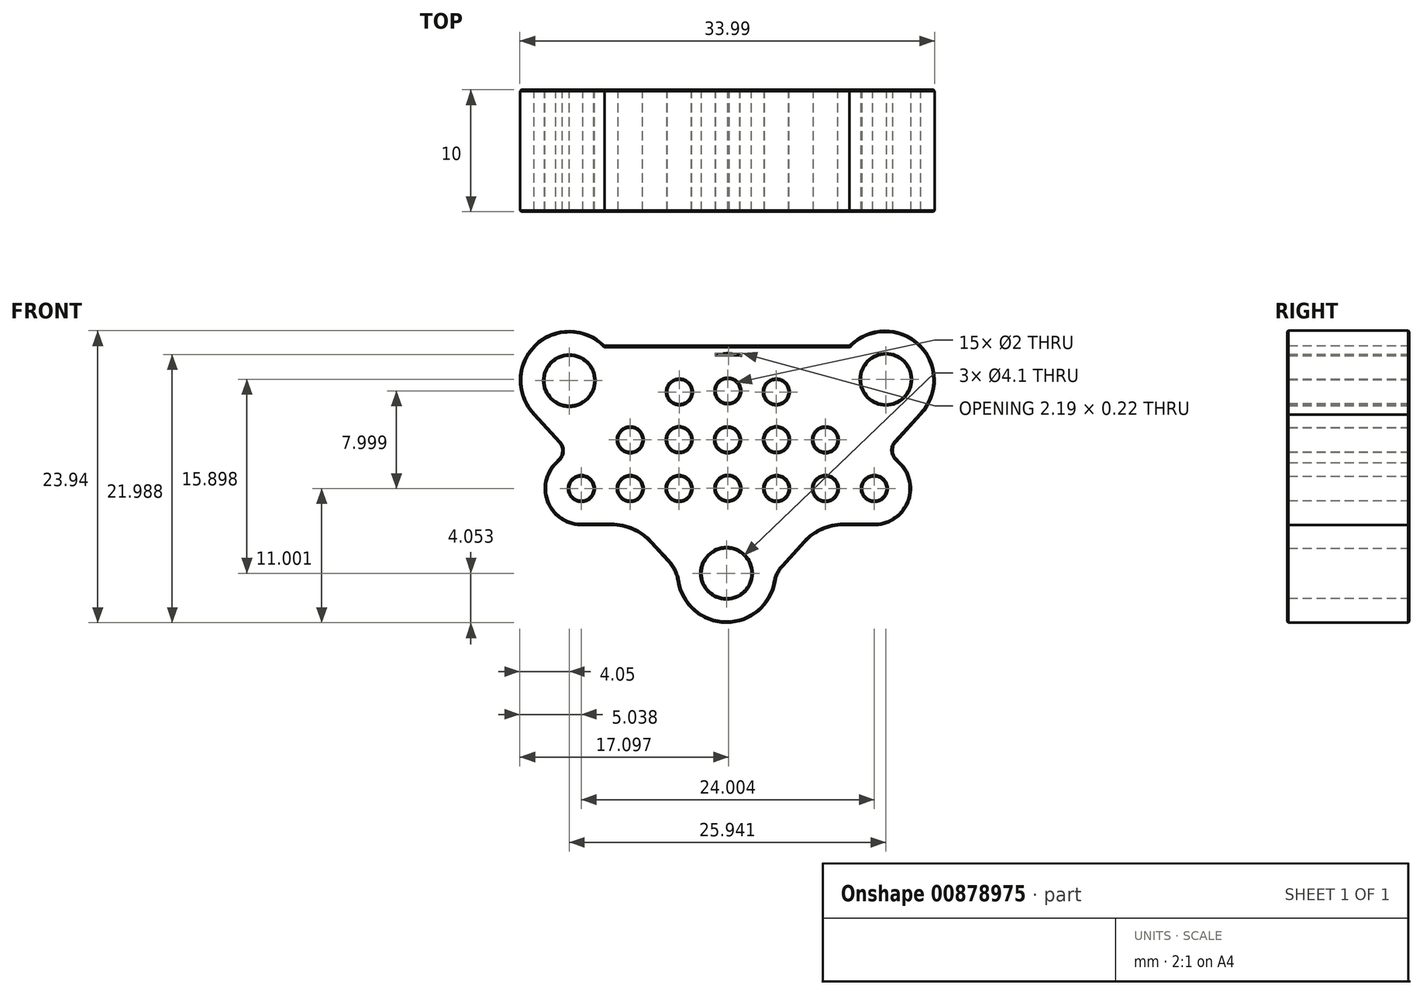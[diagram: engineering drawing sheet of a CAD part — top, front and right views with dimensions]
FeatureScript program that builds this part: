
annotation { "Feature Type Name" : "Feature", "Feature Type Description" : "" }
export const myFeature = defineFeature(function(context is Context, id is Id, definition is map)
    precondition{}
    {
        {
            var Q0;
            Q0=qCreatedBy(makeId("Front.planeOp"),FACE);
            var sketch = newSketch(context, id + "F0", { "sketchPlane" : qUnion([Q0])});
            skLineSegment(sketch, "E0", {"start": v(0, 0) * mm, "end": v(12, 0) * mm, "construction": true});
            skLineSegment(sketch, "E1.0", {"start": v(0, -4) * mm, "end": v(12, -4) * mm, "construction": true});
            skLineSegment(sketch, "E2", {"start": v(0, 4) * mm, "end": v(0, -4) * mm, "construction": true});
            skLineSegment(sketch, "E3.0", {"start": v(4, 4) * mm, "end": v(4, -4) * mm, "construction": true});
            skLineSegment(sketch, "E4.0", {"start": v(8, 4) * mm, "end": v(8, -4) * mm, "construction": true});
            skLineSegment(sketch, "E5.0", {"start": v(12, 0) * mm, "end": v(12, -4) * mm, "construction": true});
            skLineSegment(sketch, "E6.0", {"start": v(0, 4) * mm, "end": v(8, 4) * mm, "construction": true});
            skCircle(sketch, "E7", {"center": v(0, 4) * mm, "radius": 1 * mm});
            skCircle(sketch, "E8", {"center": v(3.97, 3.92) * mm, "radius": 1 * mm});
            skCircle(sketch, "E9", {"center": v(-0.03, 0) * mm, "radius": 1 * mm});
            skCircle(sketch, "E10", {"center": v(4, 0) * mm, "radius": 1 * mm});
            skCircle(sketch, "E11", {"center": v(8, 0) * mm, "radius": 1 * mm});
            skCircle(sketch, "E12", {"center": v(0, -3.98) * mm, "radius": 1 * mm});
            skCircle(sketch, "E13", {"center": v(4, -4) * mm, "radius": 1 * mm});
            skCircle(sketch, "E14", {"center": v(8, -4) * mm, "radius": 1 * mm});
            skCircle(sketch, "E15", {"center": v(12, -4) * mm, "radius": 1 * mm});
            skArc(sketch, "E16.0", {"start": v(11.88, -7) * mm, "mid": v(14.75, -5.2) * mm, "end": v(14.1, -1.86) * mm});
            skLineSegment(sketch, "E17", {"start": v(0, 7) * mm, "end": v(0.12, 7) * mm});
            skLineSegment(sketch, "E18", {"start": v(12.12, -7) * mm, "end": v(9.45, -7) * mm});
            skArc(sketch, "E19.trimOffspring", {"start": v(0.12, 7) * mm, "mid": v(0.06, 7) * mm, "end": v(0, 7) * mm});
            skCircle(sketch, "E20.MirrorC", {"center": v(-4, -4) * mm, "radius": 1 * mm});
            skCircle(sketch, "E21.MirrorC", {"center": v(-8, -4) * mm, "radius": 1 * mm});
            skCircle(sketch, "E22.MirrorC", {"center": v(-12, -4) * mm, "radius": 1 * mm});
            skLineSegment(sketch, "E23.MirrorCS", {"start": v(-4, 4) * mm, "end": v(-4, -4) * mm, "construction": true});
            skCircle(sketch, "E24.MirrorC", {"center": v(-4, 0) * mm, "radius": 1 * mm});
            skLineSegment(sketch, "E25.MirrorCS", {"start": v(-12, 0) * mm, "end": v(-12, -4) * mm, "construction": true});
            skLineSegment(sketch, "E26.MirrorCS", {"start": v(-8, 4) * mm, "end": v(-8, -4) * mm, "construction": true});
            skCircle(sketch, "E27.MirrorC", {"center": v(-3.97, 3.92) * mm, "radius": 1 * mm});
            skCircle(sketch, "E28.MirrorC", {"center": v(-8, 0) * mm, "radius": 1 * mm});
            skArc(sketch, "E29.MirrorCS", {"start": v(-11.88, -7) * mm, "mid": v(-14.75, -5.2) * mm, "end": v(-14.1, -1.86) * mm});
            skLineSegment(sketch, "E30.MirrorCS", {"start": v(-12.12, -7) * mm, "end": v(-9.54, -7) * mm});
            skPoint(sketch, "E31.orphan", {"position": v(3, -4.1) * mm});
            skPoint(sketch, "E32.0.end.orphan", {"position": v(3, -3.88) * mm});
            skPoint(sketch, "E33.MirrorCS.end.orphan", {"position": v(-3, -3.88) * mm});
            skPoint(sketch, "E33.MirrorCS.start.orphan", {"position": v(-3, -4.1) * mm});
            skLineSegment(sketch, "E34.0", {"start": v(12.1, -11) * mm, "end": v(0, -10.98) * mm});
            skCircle(sketch, "E35", {"center": v(-12.99, 4.85) * mm, "radius": 2.05 * mm});
            skCircle(sketch, "E36", {"center": v(12.95, 4.95) * mm, "radius": 2.05 * mm});
            skCircle(sketch, "E37", {"center": v(-0.1, -10.95) * mm, "radius": 2.05 * mm});
            skArc(sketch, "E38.0", {"start": v(-4.1, -11.59) * mm, "mid": v(-0.13, -15) * mm, "end": v(3.88, -11.63) * mm});
            skLineSegment(sketch, "E39", {"start": v(-10.1, 7.7) * mm, "end": v(9.97, 7.7) * mm});
            skLineSegment(sketch, "E40", {"start": v(-15.87, 2.02) * mm, "end": v(-13.82, -0.22) * mm});
            skLineSegment(sketch, "E41", {"start": v(4.5, -10.37) * mm, "end": v(6.32, -8.37) * mm});
            skLineSegment(sketch, "E42.trimOffspring", {"start": v(-13.84, -1.58) * mm, "end": v(-14.1, -1.86) * mm});
            skLineSegment(sketch, "E43.trimOffspring", {"start": v(-6.32, -8.4) * mm, "end": v(-4.88, -9.98) * mm});
            skArc(sketch, "E44.trimOffspring", {"start": v(-10.1, 7.7) * mm, "mid": v(-15.83, 7.75) * mm, "end": v(-15.87, 2.02) * mm});
            skPoint(sketch, "E45.MirrorCS.end.orphan", {"position": v(-4.03, 6.92) * mm});
            skPoint(sketch, "E45.MirrorCS.start.orphan", {"position": v(-6.26, 5.86) * mm});
            skPoint(sketch, "E46.MirrorCS.start.orphan", {"position": v(0, 7) * mm});
            skPoint(sketch, "E47.trimOffspring.end.orphan", {"position": v(4.03, 6.92) * mm});
            skPoint(sketch, "E48.orphan", {"position": v(6.26, 5.86) * mm});
            skArc(sketch, "E49.trimOffspring", {"start": v(15.81, 2.07) * mm, "mid": v(15.7, 7.8) * mm, "end": v(9.97, 7.7) * mm});
            skLineSegment(sketch, "E50.trimOffspring", {"start": v(13.8, -1.57) * mm, "end": v(14.1, -1.86) * mm});
            skLineSegment(sketch, "E51.trimOffspring", {"start": v(13.77, -0.18) * mm, "end": v(15.81, 2.07) * mm});
            skPoint(sketch, "E52.trimOffspring.end.orphan", {"position": v(0, -6.98) * mm});
            skPoint(sketch, "E53.0.start.orphan", {"position": v(-9.07, 8.7) * mm});
            skPoint(sketch, "E54.trimOffspring.end.orphan", {"position": v(-16.91, 1) * mm});
            skPoint(sketch, "E55.visualSharp", {"position": v(-13.2, -0.9) * mm});
            skArc(sketch, "E55.filletArc", {"start": v(-13.84, -1.58) * mm, "mid": v(-13.56, -0.9) * mm, "end": v(-13.82, -0.22) * mm});
            skPoint(sketch, "E56.visualSharp", {"position": v(-7.62, -6.99) * mm});
            skArc(sketch, "E56.filletArc", {"start": v(-6.32, -8.4) * mm, "mid": v(-7.78, -7.36) * mm, "end": v(-9.54, -7) * mm});
            skPoint(sketch, "E57.visualSharp", {"position": v(-4.15, -10.78) * mm});
            skArc(sketch, "E57.filletArc", {"start": v(-4.1, -11.59) * mm, "mid": v(-4.38, -10.73) * mm, "end": v(-4.88, -9.98) * mm});
            skPoint(sketch, "E58.visualSharp", {"position": v(13.12, -0.9) * mm});
            skArc(sketch, "E58.filletArc", {"start": v(13.77, -0.18) * mm, "mid": v(13.5, -0.88) * mm, "end": v(13.8, -1.57) * mm});
            skPoint(sketch, "E59.visualSharp", {"position": v(7.57, -6.99) * mm});
            skArc(sketch, "E59.filletArc", {"start": v(9.45, -7) * mm, "mid": v(7.73, -7.35) * mm, "end": v(6.32, -8.37) * mm});
            skPoint(sketch, "E60.visualSharp", {"position": v(3.94, -10.98) * mm});
            skArc(sketch, "E60.filletArc", {"start": v(4.5, -10.37) * mm, "mid": v(4.1, -10.96) * mm, "end": v(3.88, -11.63) * mm});
            skSolve(sketch);
        }
        {
            var Q0;
            Q0=qSketchRegion(id+"F0",true);
            extrude(context, id + "F1", {"entities" : qUnion([Q0]), "depth" : 10 * mm, "offsetDistance" : 25 * mm});
        }
        {
            var Q0;
            Q0=makeQuery(id+"F1.opExtrude","CAP_FACE",FACE,{"disambiguationData":[OSD([sQuery(id+"F0.wireOp",EDGE,"E7"),sQuery(id+"F0.wireOp",EDGE,"E8"),sQuery(id+"F0.wireOp",EDGE,"E9"),sQuery(id+"F0.wireOp",EDGE,"E10"),sQuery(id+"F0.wireOp",EDGE,"E11"),sQuery(id+"F0.wireOp",EDGE,"E12"),sQuery(id+"F0.wireOp",EDGE,"E13"),sQuery(id+"F0.wireOp",EDGE,"E14"),sQuery(id+"F0.wireOp",EDGE,"E15"),sQuery(id+"F0.wireOp",EDGE,"E16.0"),sQuery(id+"F0.wireOp",EDGE,"E17"),sQuery(id+"F0.wireOp",EDGE,"E18"),sQuery(id+"F0.wireOp",EDGE,"E19.trimOffspring"),sQuery(id+"F0.wireOp",EDGE,"E20.MirrorC"),sQuery(id+"F0.wireOp",EDGE,"E21.MirrorC"),sQuery(id+"F0.wireOp",EDGE,"E22.MirrorC"),sQuery(id+"F0.wireOp",EDGE,"E24.MirrorC"),sQuery(id+"F0.wireOp",EDGE,"E27.MirrorC"),sQuery(id+"F0.wireOp",EDGE,"E28.MirrorC"),sQuery(id+"F0.wireOp",EDGE,"E29.MirrorCS"),sQuery(id+"F0.wireOp",EDGE,"E30.MirrorCS"),sQuery(id+"F0.wireOp",EDGE,"E35"),sQuery(id+"F0.wireOp",EDGE,"E36"),sQuery(id+"F0.wireOp",EDGE,"E37"),sQuery(id+"F0.wireOp",EDGE,"E38.0"),sQuery(id+"F0.wireOp",EDGE,"E39"),sQuery(id+"F0.wireOp",EDGE,"E40"),sQuery(id+"F0.wireOp",EDGE,"E41"),sQuery(id+"F0.wireOp",EDGE,"E42.trimOffspring"),sQuery(id+"F0.wireOp",EDGE,"E43.trimOffspring"),sQuery(id+"F0.wireOp",EDGE,"E44.trimOffspring"),sQuery(id+"F0.wireOp",EDGE,"E49.trimOffspring"),sQuery(id+"F0.wireOp",EDGE,"E50.trimOffspring"),sQuery(id+"F0.wireOp",EDGE,"E51.trimOffspring"),sQuery(id+"F0.wireOp",EDGE,"E55.filletArc"),sQuery(id+"F0.wireOp",EDGE,"E56.filletArc"),sQuery(id+"F0.wireOp",EDGE,"E57.filletArc"),sQuery(id+"F0.wireOp",EDGE,"E58.filletArc"),sQuery(id+"F0.wireOp",EDGE,"E59.filletArc"),sQuery(id+"F0.wireOp",EDGE,"E60.filletArc")])],"isStart":false});
            chamfer(context, id + "F2", {"entities" : qUnion([Q0]), "width" : 0.1 * mm, "tangentPropagation" : true});
        }
        {
            var Q0;
            Q0=makeQuery(id+"F1.opExtrude","CAP_FACE",FACE,{"disambiguationData":[OSD([sQuery(id+"F0.wireOp",EDGE,"E7"),sQuery(id+"F0.wireOp",EDGE,"E8"),sQuery(id+"F0.wireOp",EDGE,"E9"),sQuery(id+"F0.wireOp",EDGE,"E10"),sQuery(id+"F0.wireOp",EDGE,"E11"),sQuery(id+"F0.wireOp",EDGE,"E12"),sQuery(id+"F0.wireOp",EDGE,"E13"),sQuery(id+"F0.wireOp",EDGE,"E14"),sQuery(id+"F0.wireOp",EDGE,"E15"),sQuery(id+"F0.wireOp",EDGE,"E16.0"),sQuery(id+"F0.wireOp",EDGE,"E17"),sQuery(id+"F0.wireOp",EDGE,"E18"),sQuery(id+"F0.wireOp",EDGE,"E19.trimOffspring"),sQuery(id+"F0.wireOp",EDGE,"E20.MirrorC"),sQuery(id+"F0.wireOp",EDGE,"E21.MirrorC"),sQuery(id+"F0.wireOp",EDGE,"E22.MirrorC"),sQuery(id+"F0.wireOp",EDGE,"E24.MirrorC"),sQuery(id+"F0.wireOp",EDGE,"E27.MirrorC"),sQuery(id+"F0.wireOp",EDGE,"E28.MirrorC"),sQuery(id+"F0.wireOp",EDGE,"E29.MirrorCS"),sQuery(id+"F0.wireOp",EDGE,"E30.MirrorCS"),sQuery(id+"F0.wireOp",EDGE,"E35"),sQuery(id+"F0.wireOp",EDGE,"E36"),sQuery(id+"F0.wireOp",EDGE,"E37"),sQuery(id+"F0.wireOp",EDGE,"E38.0"),sQuery(id+"F0.wireOp",EDGE,"E39"),sQuery(id+"F0.wireOp",EDGE,"E40"),sQuery(id+"F0.wireOp",EDGE,"E41"),sQuery(id+"F0.wireOp",EDGE,"E42.trimOffspring"),sQuery(id+"F0.wireOp",EDGE,"E43.trimOffspring"),sQuery(id+"F0.wireOp",EDGE,"E44.trimOffspring"),sQuery(id+"F0.wireOp",EDGE,"E49.trimOffspring"),sQuery(id+"F0.wireOp",EDGE,"E50.trimOffspring"),sQuery(id+"F0.wireOp",EDGE,"E51.trimOffspring"),sQuery(id+"F0.wireOp",EDGE,"E55.filletArc"),sQuery(id+"F0.wireOp",EDGE,"E56.filletArc"),sQuery(id+"F0.wireOp",EDGE,"E57.filletArc"),sQuery(id+"F0.wireOp",EDGE,"E58.filletArc"),sQuery(id+"F0.wireOp",EDGE,"E59.filletArc"),sQuery(id+"F0.wireOp",EDGE,"E60.filletArc")])],"isStart":true});
            chamfer(context, id + "F3", {"entities" : qUnion([Q0]), "width" : 0.1 * mm, "tangentPropagation" : true});
        }
    });
